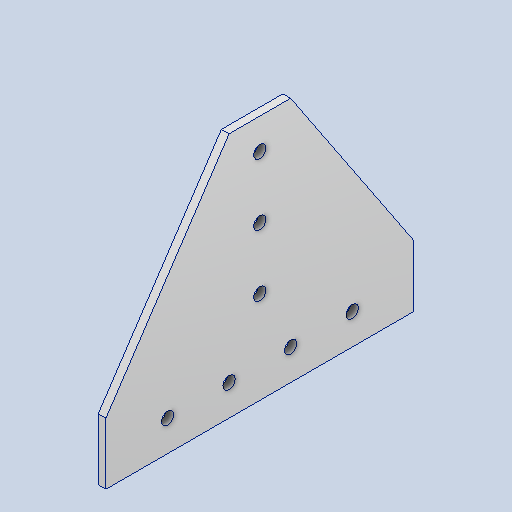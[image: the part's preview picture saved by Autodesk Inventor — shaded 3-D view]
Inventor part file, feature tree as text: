
AUTODESK INVENTOR PART (.ipt)
format: ipt  version: 2024 (Build 280153000, 153)  size: 152,576 bytes
history: native  units: in
note: dims shown in document units (in); Inventor stores cm internally (conversion verified against a paired STEP export)
features: extrude x1
ambient origin geometry x8: Origin, YZ Plane, XZ Plane, XY Plane, X Axis, Y Axis, Z Axis, Center Point
bodies: Solid1 (feature_tree)
feature tree (1):
  extrude  "Extrusion1"  Depth=1.0in
